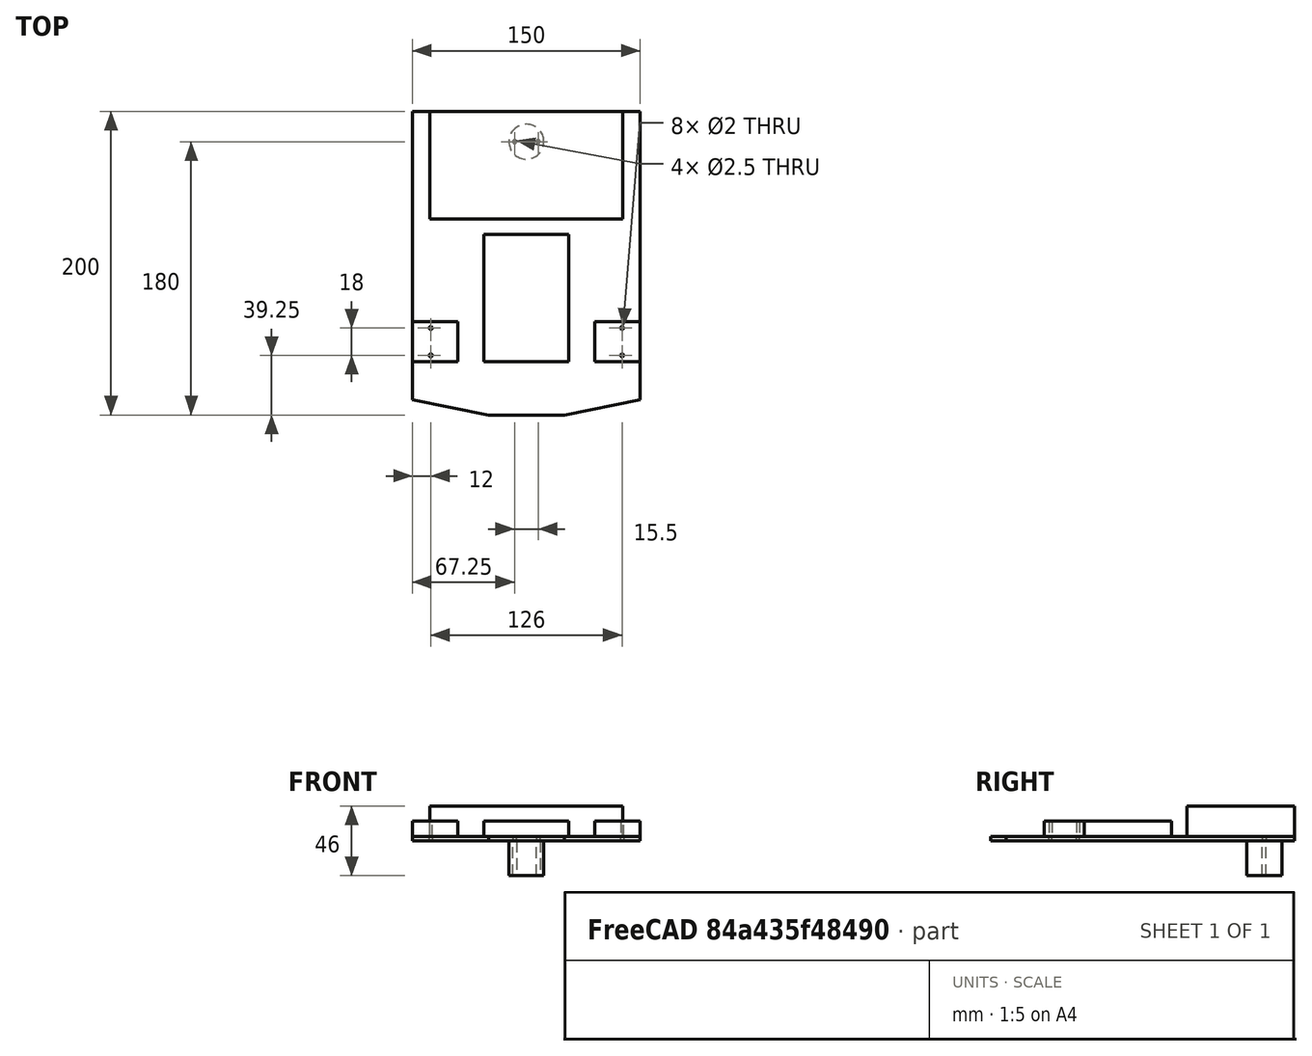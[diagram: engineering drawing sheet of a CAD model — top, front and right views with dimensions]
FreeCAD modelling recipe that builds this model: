
FCSTD DOCUMENT  (FreeCAD 0.20R28765 (Git))
Label: robot
License: All rights reserved
LicenseURL: http://en.wikipedia.org/wiki/All_rights_reserved
objects: TechDraw::DrawViewDimension×18, PartDesign::ShapeBinder×11, PartDesign::Body×7, PartDesign::Pad×6, PartDesign::Pocket×5, Sketcher::SketchObject×4, TechDraw::DrawSVGTemplate×3, TechDraw::DrawProjGroupItem×3, TechDraw::DrawProjGroup×3, TechDraw::DrawPage×3
note: 44 computed .brp shape members not serialized (recipe doc carries the construction recipe); baked Part::Feature solids carry a one-line shape summary decoded from their .brp

FEATURE [Sketcher::SketchObject] Sketch  label="ChassisOutline"
  FullyConstrained = true
  MapMode = 5
  Support = -> [XY_Plane]
  sketch-geometry (4):
    g0: LineSegment StartX=-75 StartY=100 StartZ=0 EndX=75 EndY=100 EndZ=0
    g1: LineSegment StartX=75 StartY=100 StartZ=0 EndX=75 EndY=-100 EndZ=0
    g2: LineSegment StartX=75 StartY=-100 StartZ=0 EndX=-75 EndY=-100 EndZ=0
    g3: LineSegment StartX=-75 StartY=-100 StartZ=0 EndX=-75 EndY=100 EndZ=0
  constraints (11):
    c: Coincident(g0,g1)
    c: Coincident(g3,g0)
    c: Horizontal(g0)
    c: Vertical(g1)
    c: Vertical(g3)
    c: Distance(g0) = 150
    c: DistanceY(g2,g0) = 200
    c: Coincident(g2,g1)
    c: Coincident(g2,g3)
    c: Symmetric(g1,g0,g-1)
    c: Horizontal(g2)
FEATURE [Sketcher::SketchObject] Sketch001  label="UpperParts"
  AttachmentOffset = pos=(0,0,3) rot=(0,0,1;0rad)
  ExternalGeometry = -> [Sketch]
  FullyConstrained = true
  MapMode = 5
  Placement = pos=(0,0,3) rot=(0,0,1;0rad)
  Support = -> [XY_Plane]
  sketch-geometry (21):
    g0: LineSegment StartX=-63.5 StartY=100 StartZ=0 EndX=63.5 EndY=100 EndZ=0
    g1: LineSegment StartX=63.5 StartY=100 StartZ=0 EndX=63.5 EndY=29 EndZ=0
    g2: LineSegment StartX=63.5 StartY=29 StartZ=0 EndX=-63.5 EndY=29 EndZ=0
    g3: LineSegment StartX=-63.5 StartY=29 StartZ=0 EndX=-63.5 EndY=100 EndZ=0
    g4: LineSegment StartX=-28 StartY=19 StartZ=0 EndX=28 EndY=19 EndZ=0
    g5: LineSegment StartX=28 StartY=19 StartZ=0 EndX=28 EndY=-65 EndZ=0
    g6: LineSegment StartX=28 StartY=-65 StartZ=0 EndX=-28 EndY=-65 EndZ=0
    g7: LineSegment StartX=-28 StartY=-65 StartZ=0 EndX=-28 EndY=19 EndZ=0
    g8: LineSegment StartX=-75 StartY=-65 StartZ=0 EndX=-45 EndY=-65 EndZ=0
    g9: LineSegment StartX=-45 StartY=-65 StartZ=0 EndX=-45 EndY=-38.5 EndZ=0
    g10: LineSegment StartX=-45 StartY=-38.5 StartZ=0 EndX=-75 EndY=-38.5 EndZ=0
    g11: LineSegment StartX=-75 StartY=-38.5 StartZ=0 EndX=-75 EndY=-65 EndZ=0
    g12: LineSegment StartX=75 StartY=-38.5 StartZ=0 EndX=45 EndY=-38.5 EndZ=0
    g13: LineSegment StartX=45 StartY=-38.5 StartZ=0 EndX=45 EndY=-65 EndZ=0
    g14: LineSegment StartX=45 StartY=-65 StartZ=0 EndX=75 EndY=-65 EndZ=0
    g15: LineSegment StartX=75 StartY=-65 StartZ=0 EndX=75 EndY=-38.5 EndZ=0
    g16: Circle CenterX=-63 CenterY=-42.75 CenterZ=0 NormalX=0 NormalY=0 NormalZ=1 AngleXU=0 Radius=1
    g17: Circle CenterX=-63 CenterY=-60.75 CenterZ=0 NormalX=0 NormalY=0 NormalZ=1 AngleXU=0 Radius=1
    g18: Circle CenterX=63 CenterY=-42.75 CenterZ=0 NormalX=0 NormalY=0 NormalZ=1 AngleXU=0 Radius=1
    g19: Circle CenterX=63 CenterY=-60.75 CenterZ=0 NormalX=0 NormalY=0 NormalZ=1 AngleXU=0 Radius=1
    g20: LineSegment StartX=-45 StartY=-51.75 StartZ=0 EndX=-75 EndY=-51.75 EndZ=0
  constraints (57):
    c: Coincident(g0,g1)
    c: Coincident(g1,g2)
    c: Coincident(g2,g3)
    c: Coincident(g3,g0)
    c: Horizontal(g0)
    c: Vertical(g1)
    c: Vertical(g3)
    c: PointOnObject(g0,g-3)
    c: Coincident(g4,g5)
    c: Coincident(g5,g6)
    c: Coincident(g6,g7)
    c: Coincident(g7,g4)
    c: Horizontal(g6)
    c: Vertical(g5)
    c: Vertical(g7)
    c: Distance(g3) = 71
    c: Distance(g2) = 127
    c: Distance(g6) = 56
    c: Distance(g5) = 84
    c: DistanceY(g4,g2) = 10
    c: Symmetric(g2,g1,g-2)
    c: Symmetric(g4,g4,g-2)
    c: Coincident(g8,g9)
    c: Coincident(g9,g10)
    c: Coincident(g10,g11)
    c: Coincident(g11,g8)
    c: Horizontal(g8)
    c: Horizontal(g10)
    c: Vertical(g9)
    c: Vertical(g11)
    c: PointOnObject(g8,g-4)
    c: Coincident(g12,g13)
    c: Coincident(g13,g14)
    c: Coincident(g14,g15)
    c: Coincident(g15,g12)
    c: Horizontal(g12)
    c: Horizontal(g14)
    c: Vertical(g13)
    c: Vertical(g15)
    c: PointOnObject(g12,g-5)
    c: Horizontal(g6,g8)
    c: Equal(g13,g9)
    c: Symmetric(g9,g12,g-2)
    c: DistanceX(g10,g10) = 30
    c: DistanceY(g11,g11) = 26.5
    c: PointOnObject(g20,g9)
    c: PointOnObject(g20,g11)
    c: Symmetric(g10,g8,g20)
    c: Symmetric(g16,g17,g20)
    c: Symmetric(g16,g18,g-2)
    c: Equal(g18,g19)
    c: Equal(g19,g17)
    c: Equal(g17,g16)
    c: Diameter(g16) = 2
    c: DistanceX(g20,g16) = 12
    c: Symmetric(g19,g17,g-2)
    c: DistanceY(g17,g16) = 18
FEATURE [Sketcher::SketchObject] Sketch002  label="LowerParts"
  ExternalGeometry = -> [Sketch]
  FullyConstrained = true
  MapMode = 5
  Support = -> [XY_Plane]
  sketch-geometry (3):
    g0: Circle CenterX=0 CenterY=80 CenterZ=0 NormalX=0 NormalY=0 NormalZ=1 AngleXU=0 Radius=11.5
    g1: Circle CenterX=-7.75 CenterY=80 CenterZ=0 NormalX=0 NormalY=0 NormalZ=1 AngleXU=0 Radius=1.25
    g2: Circle CenterX=7.75 CenterY=80 CenterZ=0 NormalX=0 NormalY=0 NormalZ=1 AngleXU=0 Radius=1.25
  constraints (8):
    c: PointOnObject(g0,g-2)
    c: Symmetric(g1,g2,g-2)
    c: Horizontal(g0,g1)
    c: Diameter(g2) = 2.5
    c: Equal(g2,g1)
    c: Diameter(g0) = 23
    c: DistanceX(g1,g2) = 15.5
    c: DistanceY(g0,g-3) = 20
FEATURE [PartDesign::ShapeBinder] ShapeBinder
  Support = -> [Sketch,Sketch002,Sketch001]
  TraceSupport = false
FEATURE [PartDesign::Pad] Pad
  Direction = (0,0,1)
  Length = 3
  Length2 = 10
  Profile = -> ShapeBinder
  Type = 0
FEATURE [PartDesign::ShapeBinder] ShapeBinder001
  Support = -> [Sketch001]
  TraceSupport = false
FEATURE [PartDesign::Pocket] Pocket
  BaseFeature = -> Pad
  Direction = (0,0,-1)
  Length = 5
  Length2 = 5
  Profile = -> ShapeBinder001
  Type = 1
FEATURE [PartDesign::ShapeBinder] ShapeBinder002
  Support = -> [Sketch001]
  TraceSupport = false
FEATURE [PartDesign::Pad] Pad001
  Direction = (0,0,1)
  Length = 20
  Length2 = 10
  Profile = -> ShapeBinder002
  Type = 0
FEATURE [PartDesign::Body] Body002  label="BatteryBox"
  Group = -> [ShapeBinder002,Pad001]
  Origin = -> Origin002
  Tip = -> Pad001
FEATURE [PartDesign::ShapeBinder] ShapeBinder003
  Support = -> [Sketch001]
  TraceSupport = false
FEATURE [PartDesign::Pad] Pad002
  Direction = (0,0,1)
  Length = 10
  Length2 = 10
  Profile = -> ShapeBinder003
  Type = 0
FEATURE [PartDesign::Body] Body003  label="Breadboard"
  Group = -> [ShapeBinder003,Pad002]
  Origin = -> Origin003
  Tip = -> Pad002
FEATURE [PartDesign::ShapeBinder] ShapeBinder004
  Support = -> [Sketch001]
  TraceSupport = false
FEATURE [PartDesign::Pad] Pad003
  Direction = (0,0,1)
  Length = 10
  Length2 = 10
  Profile = -> ShapeBinder004
  Type = 0
FEATURE [PartDesign::Body] Body004  label="LeftMotor"
  Group = -> [ShapeBinder004,Pad003]
  Origin = -> Origin004
  Tip = -> Pad003
FEATURE [PartDesign::ShapeBinder] ShapeBinder005
  Support = -> [Sketch001]
  TraceSupport = false
FEATURE [PartDesign::Pad] Pad004
  Direction = (0,0,1)
  Length = 10
  Length2 = 10
  Profile = -> ShapeBinder005
  Type = 0
FEATURE [PartDesign::Body] Body005  label="RightMotor"
  Group = -> [ShapeBinder005,Pad004]
  Origin = -> Origin005
  Tip = -> Pad004
FEATURE [PartDesign::ShapeBinder] ShapeBinder006
  Support = -> [Sketch001]
  TraceSupport = false
FEATURE [PartDesign::Pocket] Pocket001
  BaseFeature = -> Pocket
  Direction = (0,0,-1)
  Length = 5
  Length2 = 5
  Profile = -> ShapeBinder006
  Type = 1
FEATURE [PartDesign::ShapeBinder] ShapeBinder007
  Support = -> [Sketch002]
  TraceSupport = false
FEATURE [PartDesign::Pocket] Pocket002
  BaseFeature = -> Pocket001
  Direction = (0,0,-1)
  Length = 5
  Length2 = 5
  Profile = -> ShapeBinder007
  Reversed = true
  Type = 1
FEATURE [PartDesign::ShapeBinder] ShapeBinder008
  Support = -> [Sketch002]
  TraceSupport = false
FEATURE [PartDesign::Pad] Pad005
  Direction = (0,0,1)
  Length = 23
  Length2 = 10
  Profile = -> ShapeBinder008
  Reversed = true
  Type = 0
FEATURE [PartDesign::Body] Body006  label="Castor"
  Group = -> [ShapeBinder008,Pad005]
  Origin = -> Origin006
  Tip = -> Pad005
FEATURE [TechDraw::DrawSVGTemplate] Template
  Height = 297
  Orientation = 0
  Width = 210
FEATURE [Sketcher::SketchObject] Sketch003  label="BevelFront"
  ExternalGeometry = -> [Sketch]
  FullyConstrained = true
  MapMode = 5
  Support = -> [XY_Plane]
  sketch-geometry (6):
    g0: LineSegment StartX=-75 StartY=-90 StartZ=0 EndX=-25 EndY=-100 EndZ=0
    g1: LineSegment StartX=25 StartY=-100 StartZ=0 EndX=75 EndY=-90 EndZ=0
    g2: LineSegment StartX=-75 StartY=-90 StartZ=0 EndX=-75 EndY=-100 EndZ=0
    g3: LineSegment StartX=-25 StartY=-100 StartZ=0 EndX=-75 EndY=-100 EndZ=0
    g4: LineSegment StartX=25 StartY=-100 StartZ=0 EndX=75 EndY=-100 EndZ=0
    g5: LineSegment StartX=75 StartY=-100 StartZ=0 EndX=75 EndY=-90 EndZ=0
  constraints (14):
    c: PointOnObject(g0,g-4)
    c: PointOnObject(g0,g-3)
    c: Symmetric(g1,g0,g-2)
    c: Symmetric(g0,g1,g-2)
    c: DistanceY(g-4,g0) = 10
    c: DistanceX(g0,g1) = 50
    c: Coincident(g2,g0)
    c: Coincident(g2,g-4)
    c: Coincident(g3,g2)
    c: Coincident(g3,g0)
    c: Coincident(g1,g4)
    c: Coincident(g4,g-5)
    c: Coincident(g4,g5)
    c: Coincident(g5,g1)
FEATURE [PartDesign::Body] Body  label="SketchMain"
  Group = -> [Sketch,Sketch001,Sketch002,Sketch003]
  Origin = -> Origin
FEATURE [PartDesign::ShapeBinder] ShapeBinder009
  Support = -> [Sketch003]
  TraceSupport = false
FEATURE [PartDesign::Pocket] Pocket003
  BaseFeature = -> Pocket002
  Direction = (0,0,-1)
  Length = 5
  Length2 = 5
  Profile = -> ShapeBinder009
  Reversed = true
  Type = 1
FEATURE [PartDesign::ShapeBinder] ShapeBinder010
  Support = -> [Sketch003]
  TraceSupport = false
FEATURE [PartDesign::Pocket] Pocket004
  BaseFeature = -> Pocket003
  Direction = (0,0,-1)
  Length = 5
  Length2 = 5
  Profile = -> ShapeBinder010
  Reversed = true
  Type = 1
FEATURE [PartDesign::Body] Body001  label="ChassisPlate"
  Group = -> [ShapeBinder,Pad,ShapeBinder001,Pocket,ShapeBinder006,Pocket001,ShapeBinder007,Pocket002,ShapeBinder009,Pocket003,ShapeBinder010,Pocket004]
  Origin = -> Origin001
  Tip = -> Pocket004
FEATURE [TechDraw::DrawProjGroupItem] ProjItem  label="Front"
  CoarseView = false
  Direction = (0,0,1)
  Focus = 100
  HardHidden = false
  IsoCount = 0
  IsoHidden = false
  IsoVisible = false
  LockPosition = true
  Perspective = false
  Rotation = 0
  RotationVector = (1,0,0)
  ScaleType = 2
  SeamHidden = false
  SeamVisible = true
  SmoothHidden = false
  SmoothVisible = true
  Source = -> [Body001]
  Type = 0
  X = 0
  XDirection = (-1,-1e-16,0)
  Y = 0
FEATURE [TechDraw::DrawProjGroup] ProjGroup
  Anchor = -> ProjItem
  AutoDistribute = true
  LockPosition = false
  ProjectionType = 0
  Rotation = 0
  ScaleType = 0
  Source = -> [Body001]
  Views = -> [ProjItem]
  X = 105
  Y = 148.5
  spacingX = 15
  spacingY = 15
FEATURE [TechDraw::DrawViewDimension] Dimension
  AngleOverride = false
  Arbitrary = false
  ArbitraryTolerances = false
  EqualTolerance = true
  ExtensionAngle = 0
  FormatSpec = ⌀%.2f
  FormatSpecOverTolerance = %+.2f
  FormatSpecUnderTolerance = %+.2f
  Inverted = false
  LineAngle = 0
  LockPosition = false
  MeasureType = 1
  OverTolerance = 0
  References2D = -> [ProjItem]
  Rotation = 0
  ScaleType = 0
  TheoreticalExact = false
  Type = 5
  UnderTolerance = 0
  X = 50.1529
  Y = 70.5531
FEATURE [TechDraw::DrawViewDimension] Dimension002
  AngleOverride = false
  Arbitrary = false
  ArbitraryTolerances = false
  EqualTolerance = true
  ExtensionAngle = 0
  FormatSpec = %.2f
  FormatSpecOverTolerance = %+.2f
  FormatSpecUnderTolerance = %+.2f
  Inverted = false
  LineAngle = 0
  LockPosition = false
  MeasureType = 1
  OverTolerance = 0
  References2D = -> [ProjItem]
  Rotation = 0
  ScaleType = 0
  TheoreticalExact = false
  Type = 1
  UnderTolerance = 0
  X = 2.04208
  Y = 121.051
FEATURE [TechDraw::DrawViewDimension] Dimension004
  AngleOverride = false
  Arbitrary = false
  ArbitraryTolerances = false
  EqualTolerance = true
  ExtensionAngle = 0
  FormatSpec = %.2f
  FormatSpecOverTolerance = %+.2f
  FormatSpecUnderTolerance = %+.2f
  Inverted = false
  LineAngle = 0
  LockPosition = false
  MeasureType = 1
  OverTolerance = 0
  References2D = -> [ProjItem]
  Rotation = 0
  ScaleType = 0
  TheoreticalExact = false
  Type = 1
  UnderTolerance = 0
  X = 1.29717
  Y = 110.802
FEATURE [TechDraw::DrawViewDimension] Dimension005
  AngleOverride = false
  Arbitrary = false
  ArbitraryTolerances = false
  EqualTolerance = true
  ExtensionAngle = 0
  FormatSpec = %.2f
  FormatSpecOverTolerance = %+.2f
  FormatSpecUnderTolerance = %+.2f
  Inverted = false
  LineAngle = 0
  LockPosition = false
  MeasureType = 1
  OverTolerance = 0
  References2D = -> [ProjItem]
  Rotation = 0
  ScaleType = 0
  TheoreticalExact = false
  Type = 2
  UnderTolerance = 0
  X = 83.6298
  Y = 95.1317
FEATURE [TechDraw::DrawViewDimension] Dimension006
  AngleOverride = false
  Arbitrary = false
  ArbitraryTolerances = false
  EqualTolerance = true
  ExtensionAngle = 0
  FormatSpec = %.2f
  FormatSpecOverTolerance = %+.2f
  FormatSpecUnderTolerance = %+.2f
  Inverted = false
  LineAngle = 0
  LockPosition = false
  MeasureType = 1
  OverTolerance = 0
  References2D = -> [ProjItem]
  Rotation = 0
  ScaleType = 0
  TheoreticalExact = false
  Type = 2
  UnderTolerance = 0
  X = 86.1661
  Y = 1.23328
FEATURE [TechDraw::DrawViewDimension] Dimension007
  AngleOverride = false
  Arbitrary = false
  ArbitraryTolerances = false
  EqualTolerance = true
  ExtensionAngle = 0
  FormatSpec = %.2f
  FormatSpecOverTolerance = %+.2f
  FormatSpecUnderTolerance = %+.2f
  Inverted = false
  LineAngle = 0
  LockPosition = false
  MeasureType = 1
  OverTolerance = 0
  References2D = -> [ProjItem]
  Rotation = 0
  ScaleType = 0
  TheoreticalExact = false
  Type = 2
  UnderTolerance = 0
  X = 28.9009
  Y = -87.2406
FEATURE [TechDraw::DrawViewDimension] Dimension008
  AngleOverride = false
  Arbitrary = false
  ArbitraryTolerances = false
  EqualTolerance = true
  ExtensionAngle = 0
  FormatSpec = %.2f
  FormatSpecOverTolerance = %+.2f
  FormatSpecUnderTolerance = %+.2f
  Inverted = false
  LineAngle = 0
  LockPosition = false
  MeasureType = 1
  OverTolerance = 0
  References2D = -> [ProjItem]
  Rotation = 0
  ScaleType = 0
  TheoreticalExact = false
  Type = 1
  UnderTolerance = 0
  X = 0.423435
  Y = -60.3088
FEATURE [TechDraw::DrawViewDimension] Dimension009
  AngleOverride = false
  Arbitrary = false
  ArbitraryTolerances = false
  EqualTolerance = true
  ExtensionAngle = 0
  FormatSpec = %.2f
  FormatSpecOverTolerance = %+.2f
  FormatSpecUnderTolerance = %+.2f
  Inverted = false
  LineAngle = 0
  LockPosition = false
  MeasureType = 1
  OverTolerance = 0
  References2D = -> [ProjItem]
  Rotation = 0
  ScaleType = 0
  TheoreticalExact = false
  Type = 1
  UnderTolerance = 0
  X = -69
  Y = 72.7358
FEATURE [TechDraw::DrawViewDimension] Dimension010
  AngleOverride = false
  Arbitrary = false
  ArbitraryTolerances = false
  EqualTolerance = true
  ExtensionAngle = 0
  FormatSpec = %.2f
  FormatSpecOverTolerance = %+.2f
  FormatSpecUnderTolerance = %+.2f
  Inverted = false
  LineAngle = 0
  LockPosition = false
  MeasureType = 1
  OverTolerance = 0
  References2D = -> [ProjItem]
  Rotation = 0
  ScaleType = 0
  TheoreticalExact = false
  Type = 2
  UnderTolerance = 0
  X = -52.7358
  Y = 53.9906
FEATURE [TechDraw::DrawViewDimension] Dimension011
  AngleOverride = false
  Arbitrary = false
  ArbitraryTolerances = false
  EqualTolerance = true
  ExtensionAngle = 0
  FormatSpec = %.2f
  FormatSpecOverTolerance = %+.2f
  FormatSpecUnderTolerance = %+.2f
  Inverted = false
  LineAngle = 0
  LockPosition = false
  MeasureType = 1
  OverTolerance = 0
  References2D = -> [ProjItem]
  Rotation = 0
  ScaleType = 0
  TheoreticalExact = false
  Type = 2
  UnderTolerance = 0
  X = -53.1368
  Y = 83.3939
FEATURE [TechDraw::DrawSVGTemplate] Template001
  Height = 297
  Orientation = 0
  Width = 210
FEATURE [TechDraw::DrawProjGroupItem] ProjItem001  label="Front001"
  CoarseView = false
  Direction = (0,0,1)
  Focus = 100
  HardHidden = false
  IsoCount = 0
  IsoHidden = false
  IsoVisible = false
  LockPosition = true
  Perspective = false
  Rotation = 0
  RotationVector = (-1,0,0)
  ScaleType = 2
  SeamHidden = false
  SeamVisible = true
  SmoothHidden = false
  SmoothVisible = true
  Source = -> [Pocket002]
  Type = 0
  X = 0
  XDirection = (-1,0,0)
  Y = 0
FEATURE [TechDraw::DrawProjGroup] ProjGroup001
  Anchor = -> ProjItem001
  AutoDistribute = true
  LockPosition = false
  ProjectionType = 0
  Rotation = 0
  ScaleType = 0
  Source = -> [Pocket002]
  Views = -> [ProjItem001]
  X = 105
  Y = 148.5
  spacingX = 15
  spacingY = 15
FEATURE [TechDraw::DrawViewDimension] Dimension012
  AngleOverride = false
  Arbitrary = false
  ArbitraryTolerances = false
  EqualTolerance = true
  ExtensionAngle = 0
  FormatSpec = ⌀%.2f
  FormatSpecOverTolerance = %+.2f
  FormatSpecUnderTolerance = %+.2f
  Inverted = false
  LineAngle = 0
  LockPosition = false
  MeasureType = 1
  OverTolerance = 0
  References2D = -> [ProjItem001]
  Rotation = 0
  ScaleType = 0
  TheoreticalExact = false
  Type = 5
  UnderTolerance = 0
  X = 45.3924
  Y = 74.404
FEATURE [TechDraw::DrawViewDimension] Dimension013
  AngleOverride = false
  Arbitrary = false
  ArbitraryTolerances = false
  EqualTolerance = true
  ExtensionAngle = 0
  FormatSpec = ⌀%.2f
  FormatSpecOverTolerance = %+.2f
  FormatSpecUnderTolerance = %+.2f
  Inverted = false
  LineAngle = 0
  LockPosition = false
  MeasureType = 1
  OverTolerance = 0
  References2D = -> [ProjItem001]
  Rotation = 0
  ScaleType = 0
  TheoreticalExact = false
  Type = 5
  UnderTolerance = 0
  X = 22.3571
  Y = -61.4242
FEATURE [TechDraw::DrawPage] Page001  label="ChassisWithoutBevelsAllDimensions"
  KeepUpdated = true
  NextBalloonIndex = 1
  ProjectionType = 0
  Template = -> Template001
  Views = -> [ProjGroup001,Dimension012,Dimension013]
FEATURE [TechDraw::DrawViewDimension] Dimension014
  AngleOverride = false
  Arbitrary = false
  ArbitraryTolerances = false
  EqualTolerance = true
  ExtensionAngle = 0
  FormatSpec = ⌀%.2f
  FormatSpecOverTolerance = %+.2f
  FormatSpecUnderTolerance = %+.2f
  Inverted = false
  LineAngle = 0
  LockPosition = false
  MeasureType = 1
  OverTolerance = 0
  References2D = -> [ProjItem]
  Rotation = 0
  ScaleType = 0
  TheoreticalExact = false
  Type = 5
  UnderTolerance = 0
  X = 30.6276
  Y = -55.1297
FEATURE [TechDraw::DrawViewDimension] Dimension022
  AngleOverride = false
  Arbitrary = false
  ArbitraryTolerances = false
  EqualTolerance = true
  ExtensionAngle = 0
  FormatSpec = %.2f
  FormatSpecOverTolerance = %+.2f
  FormatSpecUnderTolerance = %+.2f
  Inverted = false
  LineAngle = 0
  LockPosition = false
  MeasureType = 1
  OverTolerance = 0
  References2D = -> [ProjItem]
  Rotation = 0
  ScaleType = 0
  TheoreticalExact = false
  Type = 1
  UnderTolerance = 0
  X = -50.6554
  Y = 111.263
FEATURE [TechDraw::DrawViewDimension] Dimension023
  AngleOverride = false
  Arbitrary = false
  ArbitraryTolerances = false
  EqualTolerance = true
  ExtensionAngle = 0
  FormatSpec = %.2f
  FormatSpecOverTolerance = %+.2f
  FormatSpecUnderTolerance = %+.2f
  Inverted = false
  LineAngle = 0
  LockPosition = false
  MeasureType = 1
  OverTolerance = 0
  References2D = -> [ProjItem]
  Rotation = 0
  ScaleType = 0
  TheoreticalExact = false
  Type = 1
  UnderTolerance = 0
  X = 50
  Y = 110.28
FEATURE [TechDraw::DrawViewDimension] Dimension024
  AngleOverride = false
  Arbitrary = false
  ArbitraryTolerances = false
  EqualTolerance = true
  ExtensionAngle = 0
  FormatSpec = %.2f
  FormatSpecOverTolerance = %+.2f
  FormatSpecUnderTolerance = %+.2f
  Inverted = false
  LineAngle = 0
  LockPosition = false
  MeasureType = 1
  OverTolerance = 0
  References2D = -> [ProjItem]
  Rotation = 0
  ScaleType = 0
  TheoreticalExact = false
  Type = 1
  UnderTolerance = 0
  X = -41.0473
  Y = -60.1593
FEATURE [TechDraw::DrawPage] Page  label="CuttingDimensions"
  KeepUpdated = true
  NextBalloonIndex = 1
  ProjectionType = 0
  Template = -> Template
  Views = -> [ProjGroup,Dimension,Dimension002,Dimension004,Dimension005,Dimension006,Dimension007,Dimension008,Dimension009,Dimension010,Dimension011,Dimension014,Dimension022,Dimension023,Dimension024]
FEATURE [TechDraw::DrawSVGTemplate] Template002
  Height = 297
  Orientation = 0
  Width = 210
FEATURE [TechDraw::DrawProjGroupItem] ProjItem002  label="Front002"
  CoarseView = false
  Direction = (0,0,1)
  Focus = 100
  HardHidden = false
  IsoCount = 0
  IsoHidden = false
  IsoVisible = false
  LockPosition = true
  Perspective = false
  Rotation = 0
  RotationVector = (-1,0,0)
  ScaleType = 2
  SeamHidden = false
  SeamVisible = true
  SmoothHidden = false
  SmoothVisible = true
  Source = -> [Body001]
  Type = 0
  X = 0
  XDirection = (-1,0,0)
  Y = 0
FEATURE [TechDraw::DrawProjGroup] ProjGroup002
  Anchor = -> ProjItem002
  AutoDistribute = true
  LockPosition = false
  ProjectionType = 0
  Rotation = 0
  ScaleType = 0
  Source = -> [Body001]
  Views = -> [ProjItem002]
  X = 105
  Y = 148.5
  spacingX = 15
  spacingY = 15
FEATURE [TechDraw::DrawViewDimension] Dimension026
  AngleOverride = false
  Arbitrary = false
  ArbitraryTolerances = false
  EqualTolerance = true
  ExtensionAngle = 0
  FormatSpec = ⌀%.2f
  FormatSpecOverTolerance = %+.2f
  FormatSpecUnderTolerance = %+.2f
  Inverted = false
  LineAngle = 0
  LockPosition = false
  MeasureType = 1
  OverTolerance = 0
  References2D = -> [ProjItem002]
  Rotation = 0
  ScaleType = 0
  TheoreticalExact = false
  Type = 5
  UnderTolerance = 0
  X = 38.1284
  Y = 75.0527
FEATURE [TechDraw::DrawViewDimension] Dimension027
  AngleOverride = false
  Arbitrary = false
  ArbitraryTolerances = false
  EqualTolerance = true
  ExtensionAngle = 0
  FormatSpec = ⌀%.2f
  FormatSpecOverTolerance = %+.2f
  FormatSpecUnderTolerance = %+.2f
  Inverted = false
  LineAngle = 0
  LockPosition = false
  MeasureType = 1
  OverTolerance = 0
  References2D = -> [ProjItem002]
  Rotation = 0
  ScaleType = 0
  TheoreticalExact = false
  Type = 5
  UnderTolerance = 0
  X = 0
  Y = -63.4854
FEATURE [TechDraw::DrawPage] Page002  label="ChassisBevelTemplate"
  KeepUpdated = true
  NextBalloonIndex = 1
  ProjectionType = 0
  Template = -> Template002
  Views = -> [ProjGroup002,Dimension026,Dimension027]
